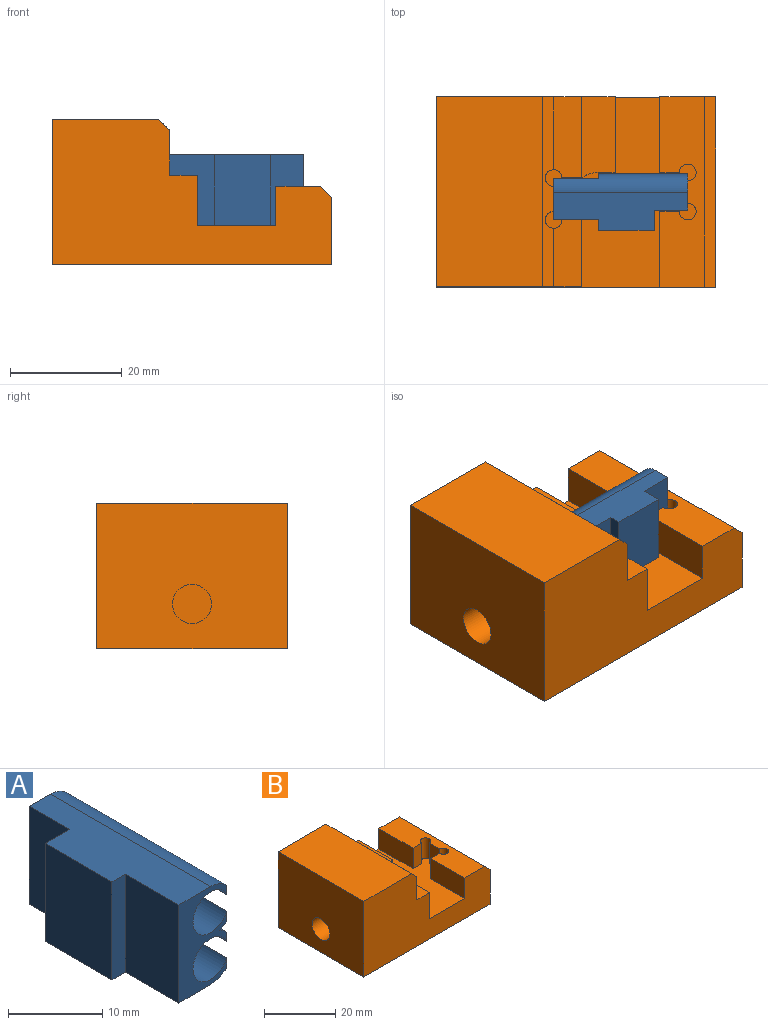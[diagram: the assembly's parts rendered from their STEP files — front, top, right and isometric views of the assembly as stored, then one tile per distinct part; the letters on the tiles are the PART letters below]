
ASSEMBLY  parts=2 mates=1
PART A: 19 faces, bbox 10.1x24x12.7 mm
  f0: plane 24x6.78mm, normal (0,0,1), area 125mm2, adj f1,f4,f7,f8,f15,f16,f17,f18
  f1: plane 12.7x10mm, normal (-1,0,0), area 127mm2, adj f0,f2,f16,f18
  f2: plane 24x6.78mm, normal (0,0,-1), area 125mm2, adj f1,f3,f7,f8,f15,f16,f17,f18
  f3: cylinder r=3.32mm len=24mm, axis (0,1,0), area 176.5mm2, adj f2,f4,f7,f8,f9,f10,f11
  f4: cylinder r=3.32mm len=24mm, axis (0,1,0), area 176.5mm2, adj f0,f3,f7,f8,f12,f13,f14
  f5: cylinder r=2.65mm len=24mm, axis (0,1,0), area 382mm2, adj f7,f8,f12,f13,f14
  f6: cylinder r=2.65mm len=24mm, axis (0,1,0), area 382mm2, adj f7,f8,f9,f10,f11
  f7: plane 12.7x7.2mm, normal (0,-1,0), area 45.7mm2, adj f0,f2,f3,f4,f5,f6,f9,f10
  f8: plane 12.7x6.5mm, normal (0,1,0), area 30.4mm2, adj f0,f2,f3,f4,f5,f6,f17
  f9: plane 8x1.21mm, normal (1,0,0), area 9.7mm2, adj f3,f6,f7,f11
  f10: plane 8x1.21mm, normal (1,0,0), area 9.7mm2, adj f3,f6,f7,f11
  f11: plane 4.55x0.9mm, normal (0,-1,0), area 2.5mm2, adj f3,f6,f9,f10
  f12: plane 4.55x0.9mm, normal (0,-1,0), area 2.5mm2, adj f4,f5,f13,f14
  f13: plane 8x1.21mm, normal (1,0,0), area 9.7mm2, adj f4,f5,f7,f12
  f14: plane 8x1.21mm, normal (1,0,0), area 9.7mm2, adj f4,f5,f7,f12
  f15: plane 12.7x8mm, normal (-1,0,0), area 101.6mm2, adj f0,f2,f7,f16
  f16: plane 12.7x2mm, normal (0,-1,0), area 25.4mm2, adj f0,f1,f2,f15
  f17: plane 12.7x6mm, normal (-1,0,0), area 76.2mm2, adj f0,f2,f8,f18
  f18: plane 12.7x3.6mm, normal (0,1,0), area 45.7mm2, adj f0,f1,f2,f17
PART B: 34 faces, bbox 50x34x26 mm
  f0: plane 13x8mm, normal (1,0,0), area 104mm2, adj f5,f22,f29,f32
  f1: plane 17x4.5mm, normal (1,0,0), area 76.5mm2, adj f3,f29,f30,f32
  f2: plane 7x3.5mm, normal (0,-1,0), area 24.5mm2, adj f3,f16,f25,f27
  f3: plane 34x27mm, normal (0,0,1), area 487.7mm2, adj f1,f2,f4,f5,f12,f13,f18,f19
  f4: plane 7x3.5mm, normal (0,1,0), area 24.5mm2, adj f3,f16,f23,f28
  f5: plane 50x26mm, normal (0,1,0), area 902mm2, adj f0,f3,f6,f8,f9,f10,f11,f16
  f6: plane 14.5x2mm, normal (1,0,0), area 29mm2, adj f5,f17,f21,f22
  f7: plane 10.5x8mm, normal (1,0,0), area 84mm2, adj f12,f20,f30,f32
  f8: plane 34x12mm, normal (1,0,0), area 408mm2, adj f5,f11,f12,f31
  f9: plane 34x19mm, normal (0,0,1), area 646mm2, adj f5,f10,f12,f32
  f10: plane 34x26mm, normal (-1,0,0), area 845.5mm2, adj f5,f9,f11,f12,f14
  f11: plane 50x34mm, normal (0,0,-1), area 1700mm2, adj f5,f8,f10,f12
  f12: plane 50x26mm, normal (0,-1,0), area 860mm2, adj f3,f7,f8,f9,f10,f11,f16,f18
  f13: plane 7x3mm, normal (0,-1,0), area 21mm2, adj f3,f17,f24,f33
  f14: cylinder r=3.5mm len=7mm, axis (-1,0,0), area 131.9mm2, adj f10,f15
  f15: plane 7x7mm, normal (-1,0,0), area 38.5mm2, adj f14
  f16: plane 34x8mm, normal (0,0,1), area 226.4mm2, adj f2,f4,f5,f12,f23,f25,f26,f27
  f17: plane 14.5x6mm, normal (0,0,1), area 82mm2, adj f5,f6,f13,f24,f33
  f18: plane 12x9mm, normal (1,0,0), area 108mm2, adj f3,f12,f19,f20
  f19: plane 9x3.5mm, normal (0,1,0), area 31.5mm2, adj f3,f18,f20,f30
  f20: plane 12x5mm, normal (0,0,1), area 58.2mm2, adj f7,f12,f18,f19,f30
  f21: plane 9x3.5mm, normal (0,-1,0), area 31.5mm2, adj f3,f6,f22,f29,f33
  f22: plane 14.5x5mm, normal (0,0,1), area 70.7mm2, adj f0,f5,f6,f21,f29
  f23: plane 13.5x7mm, normal (-1,0,0), area 94.5mm2, adj f3,f4,f12,f16
  f24: plane 13.5x7mm, normal (1,0,0), area 94.5mm2, adj f3,f5,f13,f17
  f25: plane 13.5x7mm, normal (-1,0,0), area 94.5mm2, adj f2,f3,f5,f16
  f26: plane 7x4mm, normal (-1,0,0), area 28mm2, adj f3,f16,f27,f28
  f27: cylinder r=1.5mm len=7mm, axis (0,0,1), area 49.5mm2, adj f2,f3,f16,f26
  f28: cylinder r=1.5mm len=7mm, axis (0,0,1), area 49.5mm2, adj f3,f4,f16,f26
  f29: cylinder r=1.5mm len=18.51mm, axis (0,0,1), area 105.8mm2, adj f0,f1,f3,f21,f22,f32
  f30: cylinder r=1.5mm len=18.51mm, axis (0,0,1), area 105.8mm2, adj f1,f3,f7,f19,f20,f32
  f31: plane 34x2mm, normal (0.71,0,0.71), area 96.2mm2, adj f5,f8,f12,f16
  f32: plane 34x2mm, normal (0.71,0,0.71), area 86.2mm2, adj f0,f1,f5,f7,f9,f12,f29,f30
  f33: cylinder r=5mm len=7mm, axis (0,0,1), area 22.5mm2, adj f3,f13,f17,f21
PLACE A rot(axis=(0.71,0.71,0),180deg) t=(20,-18.79,0.35)mm
PLACE B at identity fixed
MATE parallel A.f0 <-> B.f3  axis (0,0,-1) through (7.47,-19.87,-6)mm
